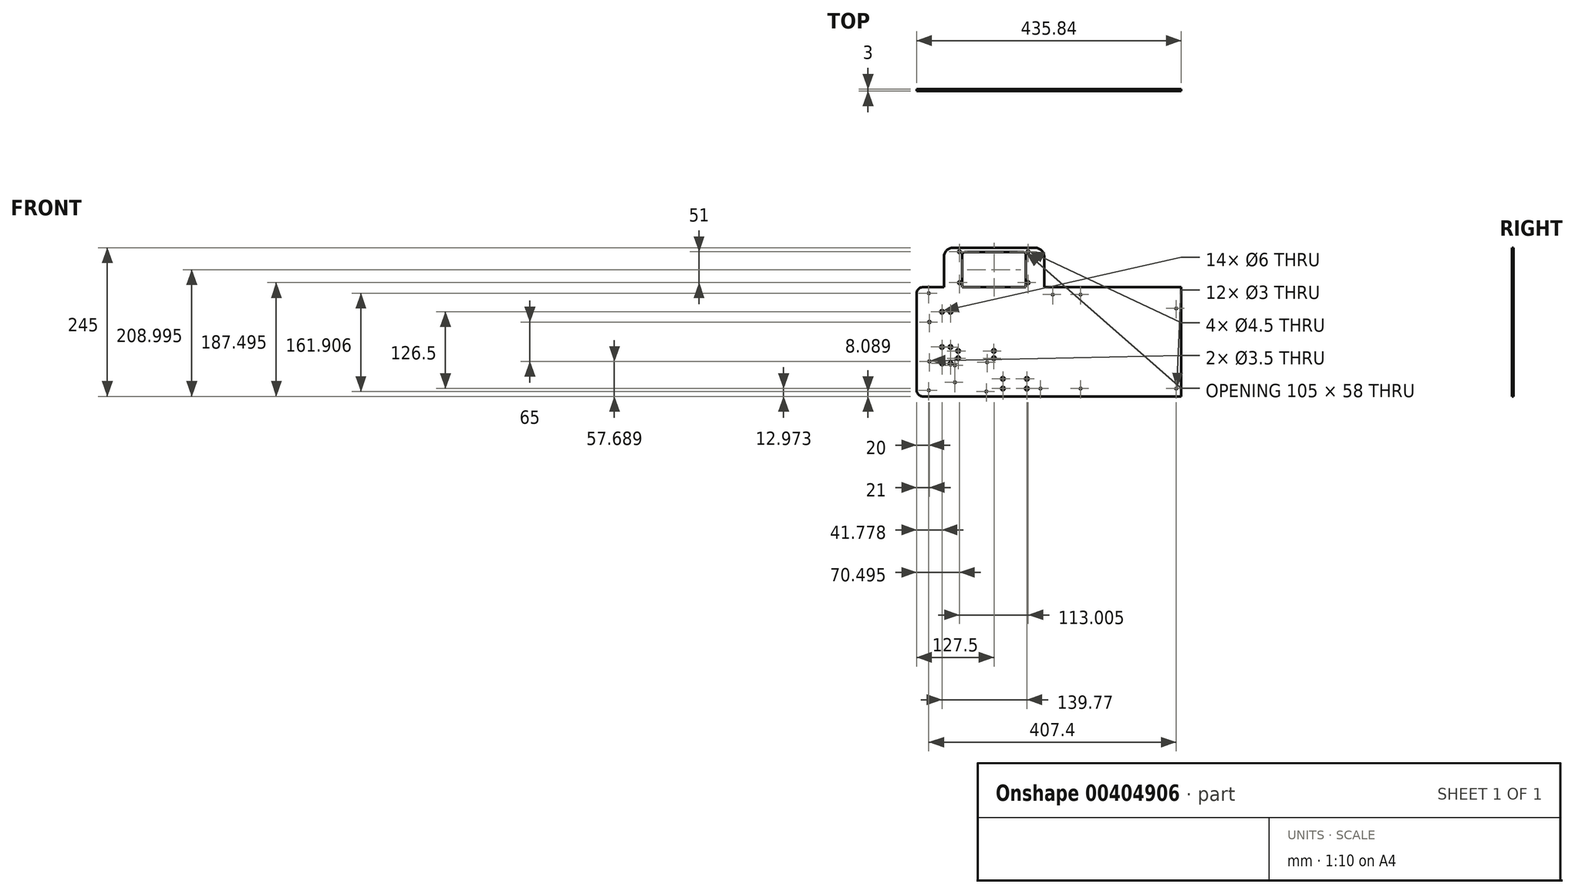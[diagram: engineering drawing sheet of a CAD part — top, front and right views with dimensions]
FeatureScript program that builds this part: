
annotation { "Feature Type Name" : "Feature", "Feature Type Description" : "" }
export const myFeature = defineFeature(function(context is Context, id is Id, definition is map)
    precondition{}
    {
        {
            var Q0;
            Q0=qCreatedBy(makeId("Front.planeOp"),FACE);
            var sketch = newSketch(context, id + "F0", { "sketchPlane" : qUnion([Q0])});
            skLineSegment(sketch, "E0.bottom", {"start": v(-224.2, 63.3) * mm, "end": v(211.64, 63.3) * mm});
            skLineSegment(sketch, "E0.top", {"start": v(-224.2, -116.7) * mm, "end": v(211.64, -116.7) * mm});
            skLineSegment(sketch, "E0.left", {"start": v(-224.2, 63.3) * mm, "end": v(-224.2, -116.7) * mm});
            skLineSegment(sketch, "E0.right", {"start": v(211.64, 63.3) * mm, "end": v(211.64, -116.7) * mm});
            skLineSegment(sketch, "E1.bottom", {"start": v(-34.2, 61.3) * mm, "end": v(209.64, 61.3) * mm});
            skLineSegment(sketch, "E1.top", {"start": v(-34.2, -111.7) * mm, "end": v(209.64, -111.7) * mm});
            skLineSegment(sketch, "E1.left", {"start": v(-34.2, 61.3) * mm, "end": v(-34.2, -111.7) * mm});
            skLineSegment(sketch, "E1.right", {"start": v(209.64, 61.3) * mm, "end": v(209.64, -111.7) * mm});
            skLineSegment(sketch, "E2", {"start": v(203.2, 61.3) * mm, "end": v(203.2, -111.7) * mm, "construction": true});
            skLineSegment(sketch, "E3", {"start": v(-34.2, 51.15) * mm, "end": v(209.64, 51.15) * mm, "construction": true});
            skLineSegment(sketch, "E4", {"start": v(-34.2, -103.7) * mm, "end": v(209.64, -103.7) * mm, "construction": true});
            skLineSegment(sketch, "E5", {"start": v(0, 61.3) * mm, "end": v(0, -111.7) * mm, "construction": true});
            skCircle(sketch, "E6", {"center": v(0, 51.15) * mm, "radius": 1.5 * mm});
            skCircle(sketch, "E7", {"center": v(45.72, 51.15) * mm, "radius": 1.5 * mm});
            skCircle(sketch, "E8", {"center": v(203.2, 28.3) * mm, "radius": 1.5 * mm});
            skCircle(sketch, "E9", {"center": v(203.2, -103.7) * mm, "radius": 1.5 * mm});
            skCircle(sketch, "E10", {"center": v(-20.32, -103.7) * mm, "radius": 1.5 * mm});
            skCircle(sketch, "E11", {"center": v(45.72, -103.7) * mm, "radius": 1.5 * mm});
            skLineSegment(sketch, "E12.bottom", {"start": v(-163.2, 63.3) * mm, "end": v(-36.2, 63.3) * mm});
            skLineSegment(sketch, "E12.top", {"start": v(-163.2, -38.7) * mm, "end": v(-36.2, -38.7) * mm});
            skLineSegment(sketch, "E12.left", {"start": v(-163.2, 63.3) * mm, "end": v(-163.2, -38.7) * mm});
            skLineSegment(sketch, "E12.right", {"start": v(-36.2, 63.3) * mm, "end": v(-36.2, -38.7) * mm});
            skLineSegment(sketch, "E13.bottom", {"start": v(-218.2, 41) * mm, "end": v(-188.2, 41) * mm});
            skLineSegment(sketch, "E13.top", {"start": v(-218.2, -89) * mm, "end": v(-188.2, -89) * mm});
            skLineSegment(sketch, "E13.left", {"start": v(-218.2, 41) * mm, "end": v(-218.2, -89) * mm});
            skLineSegment(sketch, "E13.right", {"start": v(-188.2, 41) * mm, "end": v(-188.2, -89) * mm});
            skLineSegment(sketch, "E14.bottom", {"start": v(-92.08, -56.9) * mm, "end": v(-92.08, -112.2) * mm});
            skLineSegment(sketch, "E14.top", {"start": v(-163.68, -56.9) * mm, "end": v(-163.68, -112.2) * mm});
            skLineSegment(sketch, "E14.left", {"start": v(-92.08, -56.9) * mm, "end": v(-163.68, -56.9) * mm});
            skLineSegment(sketch, "E14.right", {"start": v(-92.08, -112.2) * mm, "end": v(-163.68, -112.2) * mm});
            skCircle(sketch, "E15", {"center": v(-108.08, -60.4) * mm, "radius": 1.5 * mm});
            skCircle(sketch, "E16", {"center": v(-109.38, -108.6) * mm, "radius": 1.5 * mm});
            skCircle(sketch, "E17", {"center": v(-161.18, -65.5) * mm, "radius": 1.5 * mm});
            skCircle(sketch, "E18", {"center": v(-161.18, -93.4) * mm, "radius": 1.5 * mm});
            skLineSegment(sketch, "E19", {"start": v(-203.2, 41) * mm, "end": v(-203.2, -89) * mm, "construction": true});
            skCircle(sketch, "E20", {"center": v(-203.2, 6) * mm, "radius": 1.75 * mm});
            skCircle(sketch, "E21", {"center": v(-203.2, -59) * mm, "radius": 1.75 * mm});
            skCircle(sketch, "E22", {"center": v(-204.2, 53.3) * mm, "radius": 1.5 * mm});
            skCircle(sketch, "E23", {"center": v(-204.2, -106.7) * mm, "radius": 1.5 * mm});
            skLineSegment(sketch, "E24.bottom", {"start": v(-163.2, 63.3) * mm, "end": v(-14.2, 63.3) * mm});
            skLineSegment(sketch, "E24.top", {"start": v(-163.2, 128.3) * mm, "end": v(-29.2, 128.3) * mm});
            skLineSegment(sketch, "E24.right", {"start": v(-14.2, 63.3) * mm, "end": v(-14.2, 113.3) * mm});
            skLineSegment(sketch, "E25.bottom", {"start": v(-141.72, 63.3) * mm, "end": v(-43.6, 63.3) * mm});
            skLineSegment(sketch, "E25.top", {"start": v(-144.2, 121.3) * mm, "end": v(-49.2, 121.3) * mm});
            skLineSegment(sketch, "E26", {"start": v(-149.2, 116.3) * mm, "end": v(-149.2, 63.3) * mm});
            skLineSegment(sketch, "E27", {"start": v(-149.2, 63.3) * mm, "end": v(-44.2, 63.3) * mm});
            skLineSegment(sketch, "E28", {"start": v(-44.2, 63.3) * mm, "end": v(-44.2, 116.3) * mm});
            skLineSegment(sketch, "E29", {"start": v(-163.2, 128.3) * mm, "end": v(-164.2, 128.3) * mm});
            skLineSegment(sketch, "E30", {"start": v(-179.2, 113.3) * mm, "end": v(-179.2, 63.3) * mm});
            skPoint(sketch, "E31.visualSharp", {"position": v(-149.2, 121.3) * mm});
            skArc(sketch, "E31.filletArc", {"start": v(-144.2, 121.3) * mm, "mid": v(-147.74, 119.84) * mm, "end": v(-149.2, 116.3) * mm});
            skPoint(sketch, "E32.visualSharp", {"position": v(-44.2, 121.3) * mm});
            skArc(sketch, "E32.filletArc", {"start": v(-44.2, 116.3) * mm, "mid": v(-45.66, 119.84) * mm, "end": v(-49.2, 121.3) * mm});
            skPoint(sketch, "E33.visualSharp", {"position": v(-179.2, 128.3) * mm});
            skArc(sketch, "E33.filletArc", {"start": v(-164.2, 128.3) * mm, "mid": v(-174.8, 123.91) * mm, "end": v(-179.2, 113.3) * mm});
            skPoint(sketch, "E34.visualSharp", {"position": v(-14.2, 128.3) * mm});
            skArc(sketch, "E34.filletArc", {"start": v(-14.2, 113.3) * mm, "mid": v(-18.6, 123.91) * mm, "end": v(-29.2, 128.3) * mm});
            skCircle(sketch, "E35", {"center": v(-40.7, 70.8) * mm, "radius": 2.25 * mm});
            skCircle(sketch, "E36", {"center": v(-153.7, 70.8) * mm, "radius": 2.25 * mm});
            skCircle(sketch, "E37", {"center": v(-153.7, 121.8) * mm, "radius": 2.25 * mm});
            skCircle(sketch, "E38", {"center": v(-40.7, 121.8) * mm, "radius": 2.25 * mm});
            skLineSegment(sketch, "E39", {"start": v(-40.7, 63.3) * mm, "end": v(-40.7, 128.3) * mm, "construction": true});
            skCircle(sketch, "E40", {"center": v(-182.42, 22.78) * mm, "radius": 3 * mm});
            skCircle(sketch, "E41", {"center": v(-168.42, 22.77) * mm, "radius": 3 * mm});
            skCircle(sketch, "E42", {"center": v(-182.38, -35.25) * mm, "radius": 3 * mm});
            skCircle(sketch, "E43", {"center": v(-168.38, -35.27) * mm, "radius": 3 * mm});
            skCircle(sketch, "E44", {"center": v(-182.3, -62.43) * mm, "radius": 3 * mm});
            skCircle(sketch, "E45", {"center": v(-168.3, -62.44) * mm, "radius": 3 * mm});
            skCircle(sketch, "E46", {"center": v(-155.81, -41.77) * mm, "radius": 3 * mm});
            skCircle(sketch, "E47", {"center": v(-155.77, -53.77) * mm, "radius": 3 * mm});
            skCircle(sketch, "E48", {"center": v(-97.06, -41.69) * mm, "radius": 3 * mm});
            skCircle(sketch, "E49", {"center": v(-97.03, -53.69) * mm, "radius": 3 * mm});
            skCircle(sketch, "E50", {"center": v(-42.7, -87.72) * mm, "radius": 3 * mm});
            skCircle(sketch, "E51", {"center": v(-42.65, -103.72) * mm, "radius": 3 * mm});
            skCircle(sketch, "E52", {"center": v(-82.18, -87.68) * mm, "radius": 3 * mm});
            skCircle(sketch, "E53", {"center": v(-82.15, -103.68) * mm, "radius": 3 * mm});
            skSolve(sketch);
        }
        {
            var Q0;
            Q0=makeQuery(id+"F0.imprint","IMPRINT",FACE,{"disambiguationData":[TD([[makeQuery(id+"F0.imprint","IMPRINT",EDGE,{"derivedFrom":sQuery(id+"F0.wireOp",EDGE,"E24.top")}),-1.0]])]});
            var Q1;
            Q1=makeQuery(id+"F0.imprint","IMPRINT",FACE,{"disambiguationData":[TD([[makeQuery(id+"F0.imprint","IMPRINT",EDGE,{"derivedFrom":sQuery(id+"F0.wireOp",EDGE,"E0.top")}),1.0]])]});
            var Q2;
            Q2=makeQuery(id+"F0.imprint","IMPRINT",FACE,{"disambiguationData":[TD([[makeQuery(id+"F0.imprint","IMPRINT",EDGE,{"derivedFrom":sQuery(id+"F0.wireOp",EDGE,"E13.bottom")}),-1.0]])]});
            var Q3;
            Q3=makeQuery(id+"F0.imprint","IMPRINT",FACE,{"disambiguationData":[TD([[makeQuery(id+"F0.imprint","IMPRINT",EDGE,{"derivedFrom":sQuery(id+"F0.wireOp",EDGE,"E14.bottom")}),-1.0]])]});
            var Q4;
            {var subQ2=sQuery(id+"F0.wireOp",EDGE,"E12.left");Q4=makeQuery(id+"F0.imprint","IMPRINT",FACE,{"disambiguationData":[TD([[makeQuery(id+"F0.imprint","IMPRINT",EDGE,{"derivedFrom":subQ2}),1.0]])]});}
            var Q5;
            Q5=makeQuery(id+"F0.imprint","IMPRINT",FACE,{"disambiguationData":[TD([[makeQuery(id+"F0.imprint","IMPRINT",EDGE,{"derivedFrom":sQuery(id+"F0.wireOp",EDGE,"E1.bottom")}),-1.0]])]});
            extrude(context, id + "F1", {"entities" : qUnion([Q0, Q1, Q2, Q3, Q4, Q5]), "depth" : 3 * mm});
        }
        {
            var Q0;
            Q0=makeQuery(id+"F1.opExtrude","SWEPT_EDGE",EDGE,{"disambiguationData":[OSD([sQuery(id+"F0.wireOp",EDGE,"E0.bottom"),sQuery(id+"F0.wireOp",EDGE,"E0.left")])]});
            var Q1;
            Q1=makeQuery(id+"F1.opExtrude","SWEPT_EDGE",EDGE,{"disambiguationData":[OSD([sQuery(id+"F0.wireOp",EDGE,"E0.top"),sQuery(id+"F0.wireOp",EDGE,"E0.left")])]});
            fillet(context, id + "F2", {"entities" : qUnion([Q0, Q1]), "radius" : 10 * mm, "tangentPropagation" : true, "allowEdgeOverflow" : false});
        }
    });
